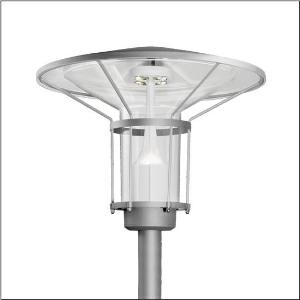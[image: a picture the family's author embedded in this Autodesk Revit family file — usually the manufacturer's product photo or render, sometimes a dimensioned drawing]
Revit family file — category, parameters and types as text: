
# Revit family: laterne_classic_iq___st1_2a_5xa5245ef14h000022_520b
name_source: partatom
category: Lighting Fixtures
units: mm (PartAtom-declared; Revit-internal decimal feet)

## family parameters
Cut with Voids When Loaded = No
Host = Face
Light Source = No
Part Type = Normal
Room Calculation Point = No
Round Connector Dimension = Use Diameter
Shared = No

## types (1)
- --- (1 x LED, 1380 lm, 10.5 W, 3000K)
    Apparent Load = 11 VA
    CIE Flux Codes = 21 60 93 97 100
    Color Rendering = 70
    Color Temperature = 3000K
    Default Elevation = 1800 mm
    Description = Lantern Classic iQ, mast luminaire, Module 540 iQ-SR, primary light control with 3 zone facetted reflector, of plastic, silver coated, highly specular, structured, primary optical cover: cover, of PMMA, transparent, light distribution: ST1.2a, light emission: direct distribution, primary light characteristic: asymmetric, installation type: post-top, LED, High Power LED, rated luminous flux: 1.380lm, luminous efficacy: 131lm/W, light colour: 730, colour temperature: 3000K, control gear: ECG iQ, control: Street-Remote, Auto-Match, Temp-Guard, Lumen-Switch, Night-Set, Smart-Wire, Light-Fading, Desk-Remote (wireless, voltage-free reading and setting of iQ features in the workshop via application-optimized NFC function/RFID function), optimised constant luminous flux control (CLO 2.0), presetting dimming logarithmic, mains connection: 230..240V, AC, 50/60Hz, connection cable pre-assembled, cable length: 5,5m, wiring characteristics: H07RN-F, start of lifetime: 11W, end of service life: 11W, reduction: 5W, luminaire housing, upper part, of glass-fibre reinforced polyester, coated, Siteco® metallic grey (DB 702S), diameter: 750mm, height: 596mm, spigot size: d x l = 76 x 70mm (post-top) | with reducer (optional accessory) 60 x 70mm, post-top mast mounting element, of diecast aluminium, coated, Siteco® metallic grey (DB 702S), Module 540 iQ-SR, traffic white (RAL 9016), equipment: standard, protection rating (complete): IP65, insulation class (complete): insulation class II (safety insulation), certification: CE, ENEC, VDE, packaging unit: 1 piece

Light Distribution: ST1.2a
    Height = 596 mm
    Lamp = 1 x LED
    Lamp Light Flux = 1380 lm
    Lamp Power = 10.5 W
    Lamp count = 1
    Length = 750 mm
    Luminous efficacy = 131 lm/W
    Manufacturer = Siteco
    ModVariant = No
    Model = 5XA5245EF14H000022
    Number of Poles = 1
    OnlyDefault = Yes
    Power Factor = 1
    Product Name = Laterne Classic iQ | ST1.2a
    Product group = mast luminaire | pylon top
    ProductGroupID = 6100
    Protection Class = Protection class II
    Protection Degree = IP 65
    RLX_Detail_Level = 1
    RLX_Emergency_Light_Flux = 0 lm
    RLX_Emergency_Type = 0
    RLX_Emergency_Type_DB = No
    RlxData = <blob elided: 64245 chars, md5=099f1926>
    Socket = socket
    Standby Power = 0 W
    System Light Flux = 1380 lm
    System Power = 11 W
    Type Comments = factory setting: luminous flux: 100 % | dim-lin: 254 | 419 mA
    Type Image = l_1006052.jpg
    URL = http://relux.com
    VarID = @adj_092635
    Voltage = 0 V
    Weight = 0.00 kg
    Width = 0 mm  [stored 0 ft]

note: [stored X ft] marks values corroborated as IEEE doubles in the binary element streams (Revit-internal decimal feet)

## geometry (parser evidence)
native form markers: Blend x4, Sweep x10
no freeform markers — native parametric forms only
